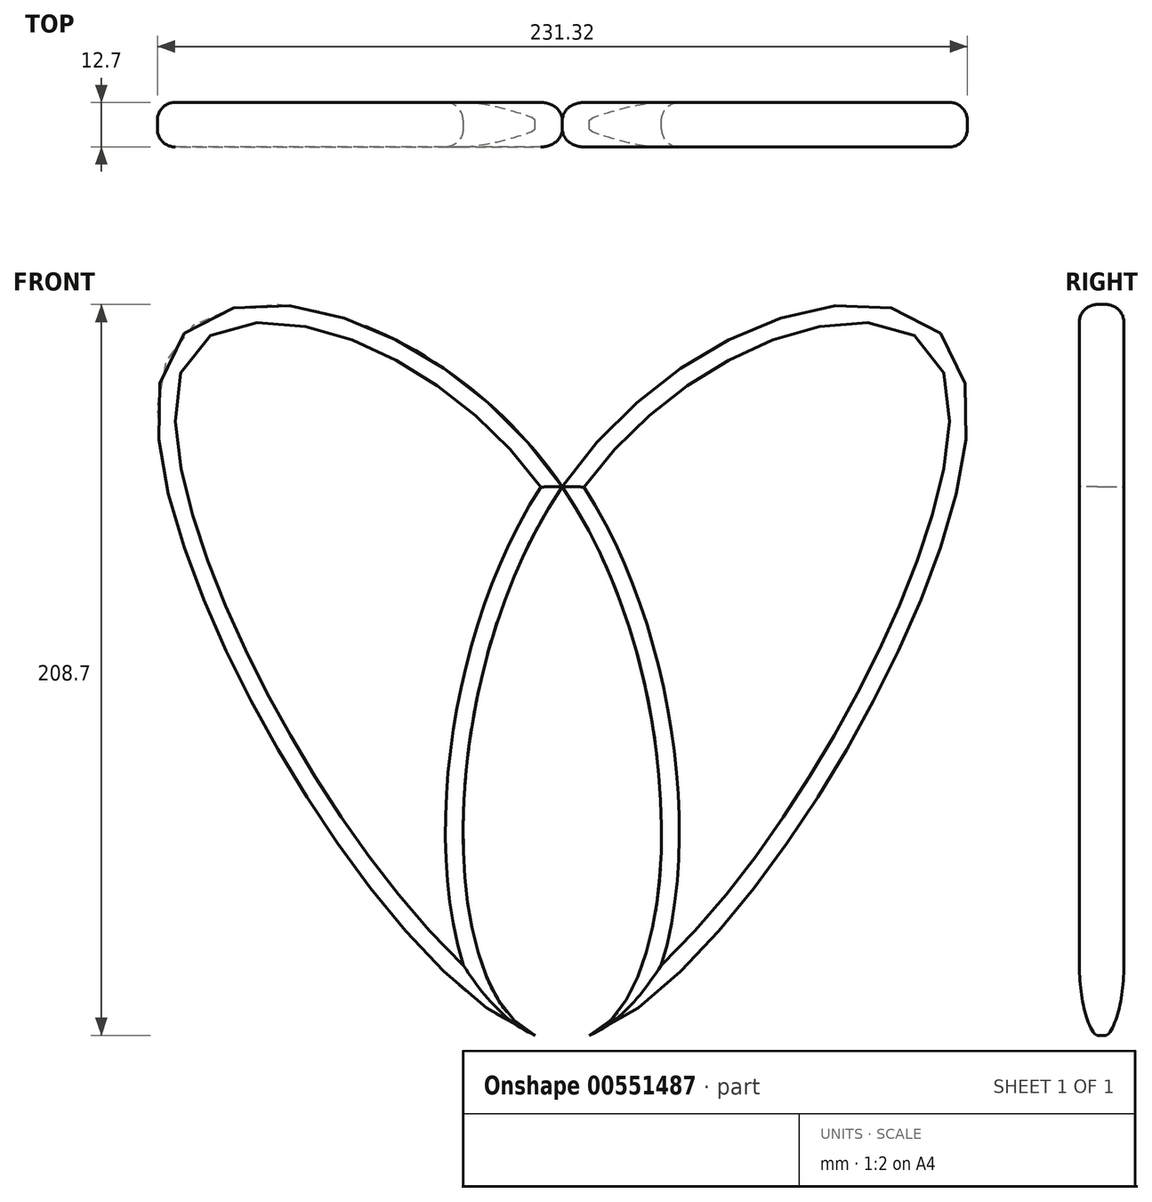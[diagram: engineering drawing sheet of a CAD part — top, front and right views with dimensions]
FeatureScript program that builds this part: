
annotation { "Feature Type Name" : "Feature", "Feature Type Description" : "" }
export const myFeature = defineFeature(function(context is Context, id is Id, definition is map)
    precondition{}
    {
        {
            var Q0;
            Q0=qCreatedBy(makeId("Front.planeOp"),FACE);
            var sketch = newSketch(context, id + "F0", { "sketchPlane" : qUnion([Q0])});
            skLineSegment(sketch, "E0", {"start": v(0, 76.68) * mm, "end": v(0, -81.55) * mm});
            skFitSpline(sketch, "E1", {"points": [v(0, 76.68) * mm, v(113.62, 111.36) * mm, v(0, -81.55) * mm, v(0, 76.68) * mm]});
            skFitSpline(sketch, "E2.MirrorC", {"points": [v(0, 76.68) * mm, v(-113.62, 111.36) * mm, v(0, -81.55) * mm, v(0, 76.68) * mm]});
            skPoint(sketch, "E3.1.internal.snap0", {"position": v(0, -2.43) * mm});
            skPoint(sketch, "E3.3.internal.snap0", {"position": v(0, -2.43) * mm});
            skPoint(sketch, "E3.0.internal.orphan", {"position": v(0, 62.47) * mm});
            skPoint(sketch, "E3.1.internal.orphan", {"position": v(15.82, -2.43) * mm});
            skPoint(sketch, "E3.2.internal.orphan", {"position": v(0, -76.7) * mm});
            skPoint(sketch, "E3.3.internal.orphan", {"position": v(-17.1, -2.43) * mm});
            skSolve(sketch);
        }
        {
            var Q0;
            {var subQ0=sQuery(id+"F0.wireOp",EDGE,"E2.MirrorC");var subQ1=sQuery(id+"F0.wireOp",EDGE,"E1");var subQ3=makeQuery(id+"F0.imprint","INTERSECT",VERTEX,{"disambiguationData":[OD(0.0)],"derivedFrom":[subQ1,subQ0]});Q0=makeQuery(id+"F0.imprint","IMPRINT",FACE,{"disambiguationData":[TD([[makeQuery(id+"F0.imprint","IMPRINT",EDGE,{"disambiguationData":[TD([[subQ3,1.0]])],"derivedFrom":subQ1}),-1.0]])]});}
            extrude(context, id + "F1", {"entities" : qUnion([Q0]), "depth" : 6.35 * mm, "offsetDistance" : 25.4 * mm, "hasSecondDirection" : true, "secondDirectionOppositeDirection" : true, "secondDirectionDepth" : 6.35 * mm});
        }
        {
            var Q0;
            {var subQ0=sQuery(id+"F0.wireOp",EDGE,"E2.MirrorC");var subQ1=sQuery(id+"F0.wireOp",EDGE,"E1");var subQ3=makeQuery(id+"F0.imprint","INTERSECT",VERTEX,{"disambiguationData":[OD(1.0)],"derivedFrom":[subQ1,subQ0]});Q0=makeQuery(id+"F0.imprint","IMPRINT",FACE,{"disambiguationData":[TD([[makeQuery(id+"F0.imprint","IMPRINT",EDGE,{"disambiguationData":[TD([[subQ3,-1.0]])],"derivedFrom":subQ1}),1.0]])]});}
            extrude(context, id + "F2", {"entities" : qUnion([Q0]), "depth" : 6.35 * mm, "offsetDistance" : 25.4 * mm, "hasSecondDirection" : true, "secondDirectionOppositeDirection" : true, "secondDirectionDepth" : 6.35 * mm});
        }
        {
            var Q0;
            Q0=makeQuery(id+"F1.opExtrude","CAP_EDGE",EDGE,{"disambiguationData":[OSD([sQuery(id+"F0.wireOp",EDGE,"E1")])],"isStart":true});
            var Q1;
            Q1=makeQuery(id+"F2.opExtrude","CAP_EDGE",EDGE,{"disambiguationData":[OSD([sQuery(id+"F0.wireOp",EDGE,"E2.MirrorC")])],"isStart":false});
            var Q2;
            Q2=makeQuery(id+"F2.opExtrude","CAP_EDGE",EDGE,{"disambiguationData":[OSD([sQuery(id+"F0.wireOp",EDGE,"E2.MirrorC")])],"isStart":true});
            var Q3;
            Q3=makeQuery(id+"F2.opExtrude","CAP_EDGE",EDGE,{"disambiguationData":[OSD([sQuery(id+"F0.wireOp",EDGE,"E1")])],"isStart":true});
            var Q4;
            Q4=makeQuery(id+"F1.opExtrude","CAP_EDGE",EDGE,{"disambiguationData":[OSD([sQuery(id+"F0.wireOp",EDGE,"E2.MirrorC")])],"isStart":true});
            var Q5;
            Q5=makeQuery(id+"F1.opExtrude","CAP_FACE",FACE,{"disambiguationData":[OSD([sQuery(id+"F0.wireOp",EDGE,"E1"),sQuery(id+"F0.wireOp",EDGE,"E2.MirrorC")])],"isStart":false});
            var Q6;
            Q6=makeQuery(id+"F2.opExtrude","CAP_EDGE",EDGE,{"disambiguationData":[OSD([sQuery(id+"F0.wireOp",EDGE,"E1")])],"isStart":false});
            var Q7;
            Q7=makeQuery(id+"F1.opExtrude","CAP_EDGE",EDGE,{"disambiguationData":[OSD([sQuery(id+"F0.wireOp",EDGE,"E1")])],"isStart":false});
            fillet(context, id + "F3", {"entities" : qUnion([Q0, Q1, Q2, Q3, Q4, Q5, Q6, Q7]), "radius" : 5.08 * mm, "tangentPropagation" : true, "allowEdgeOverflow" : false});
        }
    });
